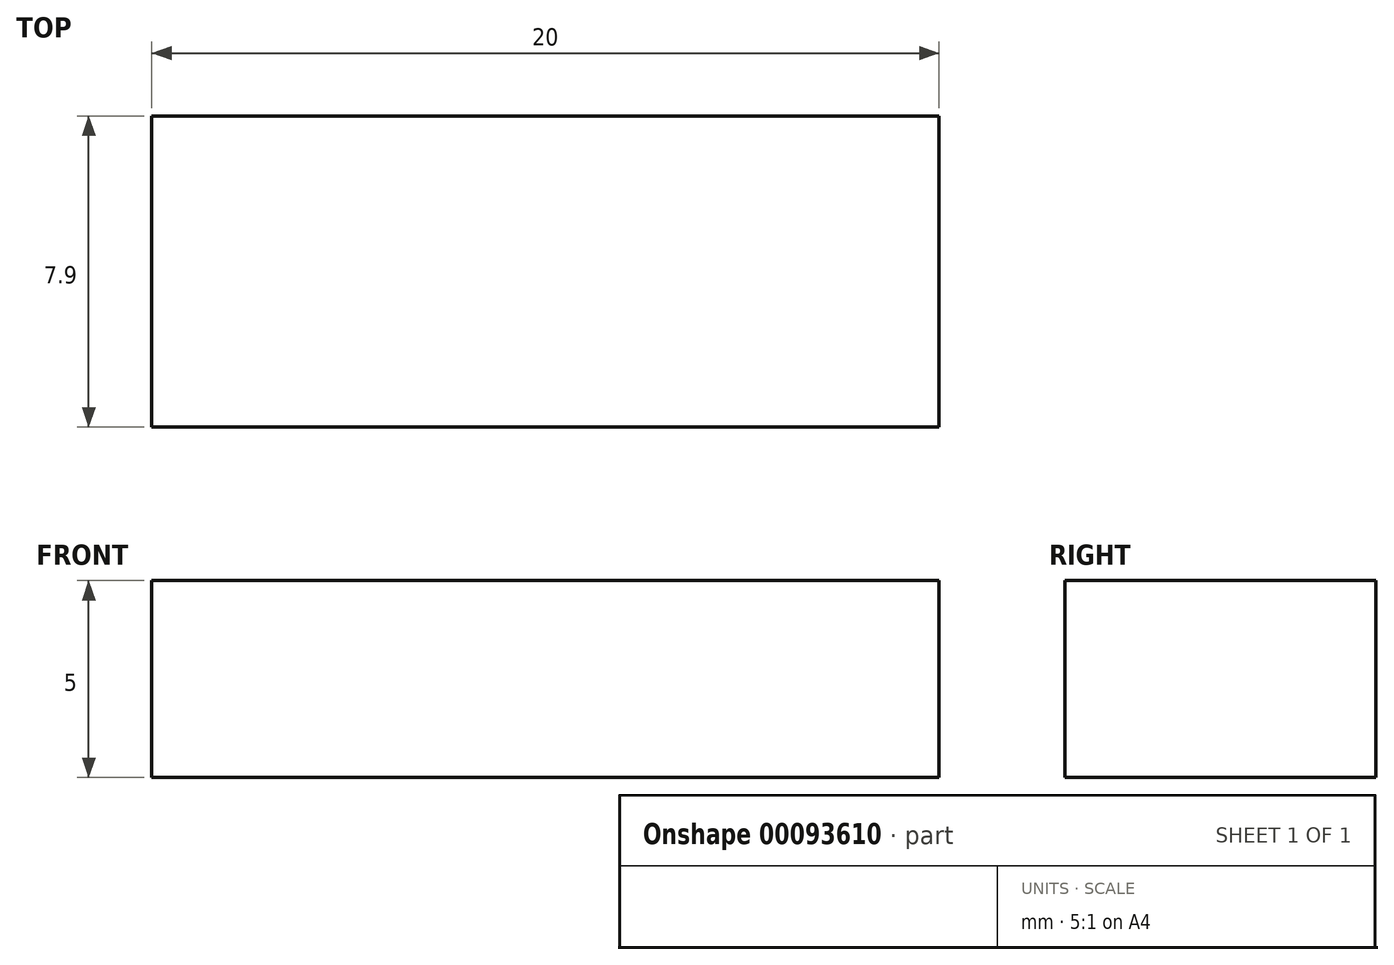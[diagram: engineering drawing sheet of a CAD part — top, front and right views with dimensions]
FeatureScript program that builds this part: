
annotation { "Feature Type Name" : "Feature", "Feature Type Description" : "" }
export const myFeature = defineFeature(function(context is Context, id is Id, definition is map)
    precondition{}
    {
        {
            var Q0;
            Q0=qCreatedBy(makeId("Top.planeOp"),FACE);
            var sketch = newSketch(context, id + "F0", { "sketchPlane" : qUnion([Q0])});
            skLineSegment(sketch, "E0.bottom", {"start": v(0, 0) * mm, "end": v(-20, 0) * mm});
            skLineSegment(sketch, "E0.top", {"start": v(0, 7.9) * mm, "end": v(-20, 7.9) * mm});
            skLineSegment(sketch, "E0.left", {"start": v(0, 0) * mm, "end": v(0, 7.9) * mm});
            skLineSegment(sketch, "E0.right", {"start": v(-20, 0) * mm, "end": v(-20, 7.9) * mm});
            skSolve(sketch);
        }
        {
            var Q0;
            Q0 = qSketchRegion(id + "F0", true);
            extrude(context, id + "F1", {"entities" : qUnion([Q0]), "depth" : 5 * mm});
        }
    });
